# Revit family: 121611001 Sanitario Nyren bco
name_source: partatom
category: Plumbing Fixtures
units: mm (PartAtom-declared; Revit-internal decimal feet)

## family parameters
Always vertical = Yes
Cut with Voids When Loaded = No
Host = Floor
Part Type = Normal
Room Calculation Point = No
Round Connector Dimension = Use Diameter
Shared = No

## types (1)
- 121611001 Sanitario Nyren bco
    Acabado = <By Category>
    Capacidad de descarga = 500 g
    Consumo de agua = 48 lt
    Creado por = IDD
    Description = El sanitario inteligente Nyren, le dará a tu baño el más alto grado de estética y elegancia futurista, el cual podrás accionar con su novedoso control remoto que gracias a su asiento asegurarás una experiencia única ¡Cónocelo ahora!
    Dimensiones generales producto (H * W * D) = 474 cm x 691 cm x 414 cm
    Fecha de creación = 09/10/2020
    Garantía = Garantía Integral Corona en porcelana sanitaria
    Garantía de otros componentes = 5 años en grifería y asiento
    Manufacturer = Corona
    Material = Corona_Porcelana_Sanitaria_Blanco
    Sistema de descarga = Botón tipo push
    Tipo de Válvula = Válvula doble de descarga
    URL = https://corona.co
    Uso = Residencial

## geometry (parser evidence)
native form markers: Sweep x5
no freeform markers — native parametric forms only
